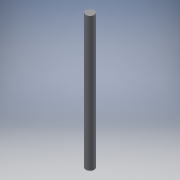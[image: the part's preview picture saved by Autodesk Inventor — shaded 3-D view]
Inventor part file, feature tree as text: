
AUTODESK INVENTOR PART (.ipt)
format: ipt  version: 2018 (Build 220112000, 112)  size: 88,064 bytes
history: native  units: mm
features: extrude x1, sketch x1
ambient origin geometry x8: Origin, YZ Plane, XZ Plane, XY Plane, X Axis, Y Axis, Z Axis, Center Point
bodies: Solid1 (feature_tree)
feature tree (2):
  extrude  "Extrusion1"  Depth=400.0mm TaperAngle=0.0deg
  sketch  "Sketch1"  dims[d0=25.0mm d1=400.0mm d2=0.0mm]
